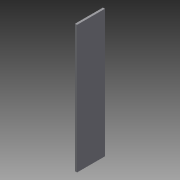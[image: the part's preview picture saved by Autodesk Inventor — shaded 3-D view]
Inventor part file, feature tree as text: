
AUTODESK INVENTOR PART (.ipt)
format: ipt  version: 2014 (Build 180170000, 170)  size: 66,048 bytes
history: native  units: in
note: dims shown in document units (in); Inventor stores cm internally (conversion verified against a paired STEP export)
features: extrude x1, sketch x1
ambient origin geometry x8: Origin, YZ Plane, XZ Plane, XY Plane, X Axis, Y Axis, Z Axis, Center Point
bodies: Solid1 (feature_tree)
feature tree (2):
  extrude  "Extrusion1"  Depth=3.5in
  sketch  "Sketch1"  dims[d0=16.0in d2=3.5in d3=0.25in d4=0.0in]
